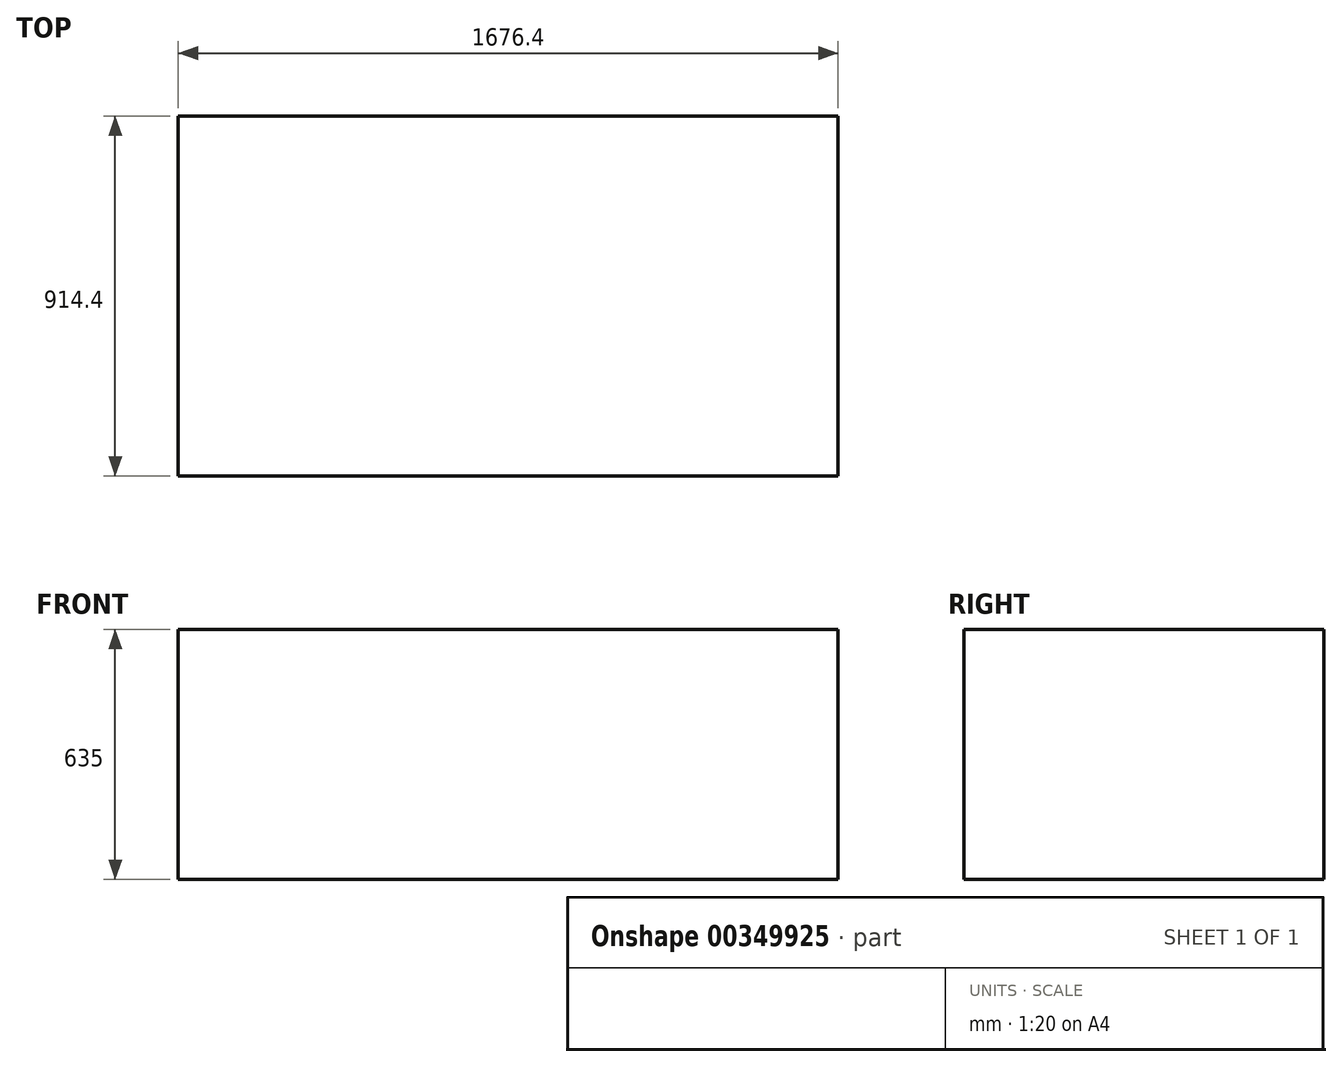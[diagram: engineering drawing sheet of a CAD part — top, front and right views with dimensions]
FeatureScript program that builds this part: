
annotation { "Feature Type Name" : "Feature", "Feature Type Description" : "" }
export const myFeature = defineFeature(function(context is Context, id is Id, definition is map)
    precondition{}
    {
        {
            var Q0;
            Q0=qCreatedBy(makeId("Front.planeOp"),FACE);
            var sketch = newSketch(context, id + "F0", { "sketchPlane" : qUnion([Q0])});
            skLineSegment(sketch, "E0.bottom", {"start": v(841.02, -317.5) * mm, "end": v(-835.38, -317.5) * mm});
            skLineSegment(sketch, "E0.top", {"start": v(841.02, 317.5) * mm, "end": v(-835.38, 317.5) * mm});
            skLineSegment(sketch, "E0.left", {"start": v(841.02, -317.5) * mm, "end": v(841.02, 317.5) * mm});
            skLineSegment(sketch, "E0.right", {"start": v(-835.38, -317.5) * mm, "end": v(-835.38, 317.5) * mm});
            skPoint(sketch, "E0.middle", {"position": v(2.82, 0) * mm});
            skSolve(sketch);
        }
        {
            var Q0;
            Q0 = qSketchRegion(id + "F0", true);
            extrude(context, id + "F1", {"entities" : qUnion([Q0]), "depth" : 914.4 * mm, "offsetDistance" : 25.4 * mm});
        }
    });
